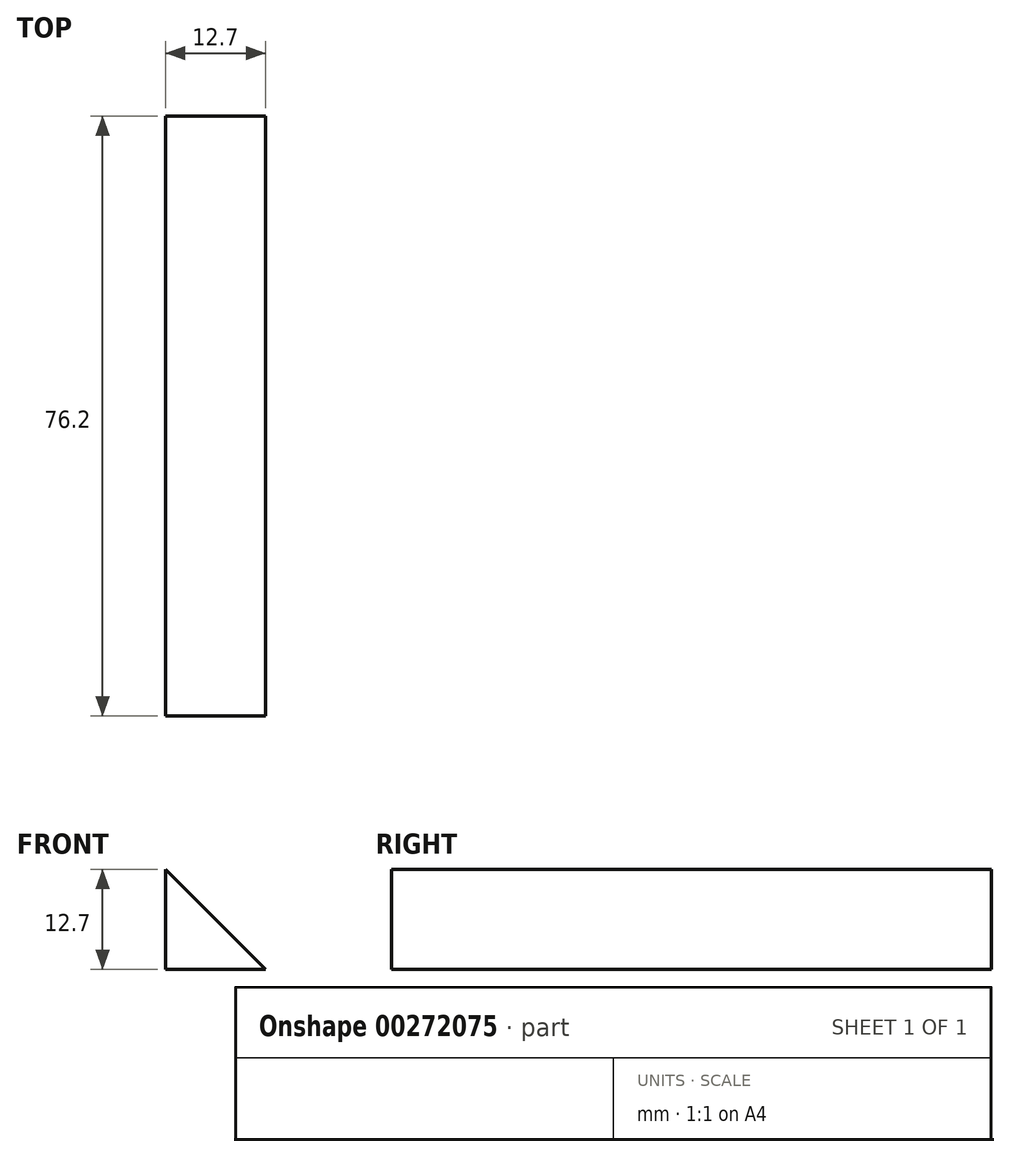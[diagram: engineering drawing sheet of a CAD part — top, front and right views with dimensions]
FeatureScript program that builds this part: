
annotation { "Feature Type Name" : "Feature", "Feature Type Description" : "" }
export const myFeature = defineFeature(function(context is Context, id is Id, definition is map)
    precondition{}
    {
        {
            var Q0;
            Q0=qCreatedBy(makeId("Front.planeOp"),FACE);
            var sketch = newSketch(context, id + "F0", { "sketchPlane" : qUnion([Q0])});
            skLineSegment(sketch, "E0.bottom", {"start": v(-188.24, 0) * mm, "end": v(-200.94, 0) * mm});
            skLineSegment(sketch, "E0.top", {"start": v(-188.24, 12.7) * mm, "end": v(-200.94, 12.7) * mm});
            skLineSegment(sketch, "E0.left", {"start": v(-188.24, 0) * mm, "end": v(-188.24, 12.7) * mm});
            skLineSegment(sketch, "E0.right", {"start": v(-200.94, 0) * mm, "end": v(-200.94, 12.7) * mm});
            skPoint(sketch, "E0.middle", {"position": v(-194.59, 6.35) * mm});
            skSolve(sketch);
        }
        {
            var Q0;
            Q0=makeQuery(id+"F0.imprint","IMPRINT",FACE,{"disambiguationData":[TD([[makeQuery(id+"F0.imprint","IMPRINT",EDGE,{"derivedFrom":sQuery(id+"F0.wireOp",EDGE,"E0.bottom")}),-1.0]])]});
            extrude(context, id + "F1", {"entities" : qUnion([Q0]), "depth" : 76.2 * mm});
        }
        {
            var Q0;
            Q0=makeQuery(id+"F1.opExtrude","SWEPT_EDGE",EDGE,{"disambiguationData":[OSD([sQuery(id+"F0.wireOp",EDGE,"E0.top"),sQuery(id+"F0.wireOp",EDGE,"E0.left")])]});
            chamfer(context, id + "F2", {"entities" : qUnion([Q0]), "width" : 12.7 * mm, "tangentPropagation" : true});
        }
    });
